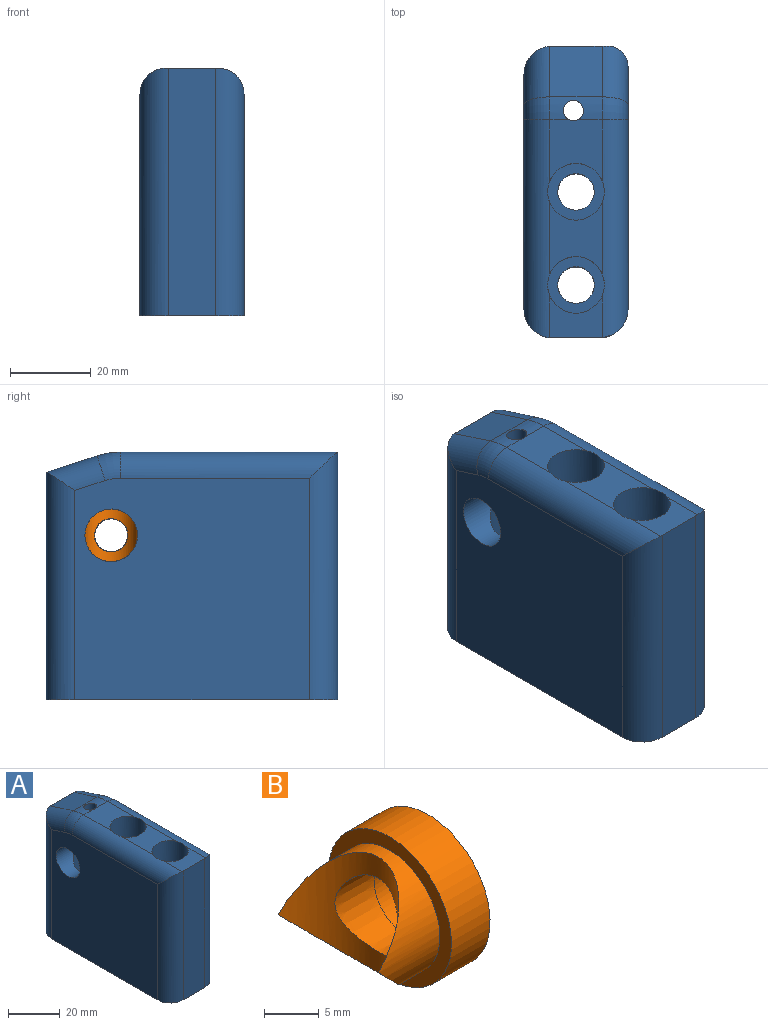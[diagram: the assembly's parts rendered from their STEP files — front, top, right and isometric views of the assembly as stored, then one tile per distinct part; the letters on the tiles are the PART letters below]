
ASSEMBLY  parts=2 mates=1
PART A: 32 faces, bbox 25.7x72.1x61.3 mm
  f0: cylinder r=6.5mm len=20.6mm, axis (1,0,0), area 651.4mm2, adj f1,f28,f29,f30,f31
  f1: cylinder r=2.5mm len=14mm, axis (0,0,-1), area 218.8mm2, adj f0,f2,f27
  f2: plane 15.04x12.9mm, normal (0,0,1), area 153.9mm2, adj f1,f3,f25,f26,f27
  f3: cylinder r=6.4mm len=53.73mm, axis (0,-1,0), area 505.1mm2, adj f2,f4,f19,f21,f22,f23,f24,f25
  f4: torus R=12mm, axis (-1,0,0), area 50.6mm2, adj f3,f5,f19,f27
  f5: cylinder r=6.4mm len=14.61mm, axis (0,-0.95,0.31), area 123.6mm2, adj f4,f6,f17,f18,f19
  f6: plane 12.9x12.58mm, normal (0,0.31,0.95), area 170.5mm2, adj f5,f7,f9,f17,f27
  f7: cylinder r=6.4mm len=14.52mm, axis (0,0.95,-0.31), area 106.2mm2, adj f6,f8,f9,f31
  f8: torus R=12mm, axis (1,0,0), area 50.6mm2, adj f7,f26,f27,f31
  f9: cylinder r=7mm len=56.14mm, axis (0,0,-1), area 600.7mm2, adj f6,f7,f10,f17,f31
  f10: plane 72x25.7mm, normal (0,0,-1), area 1553.5mm2, adj f9,f11,f13,f15,f16,f17,f18,f19
  f11: cylinder r=4.5mm len=45mm, axis (0,0,-1), area 1272.3mm2, adj f10,f12
  f12: plane 14x14mm, normal (0,0,1), area 90.3mm2, adj f11,f25
  f13: cylinder r=4.5mm len=45mm, axis (0,0,-1), area 1272.3mm2, adj f10,f14
  f14: plane 14x14mm, normal (0,0,1), area 90.3mm2, adj f13,f23
  f15: cylinder r=7mm len=61.09mm, axis (0,0,-1), area 647.4mm2, adj f10,f16,f22,f26,f31
  f16: plane 61.09x11.7mm, normal (0,-1,0), area 714.8mm2, adj f10,f15,f21,f22
  f17: plane 56.15x13.73mm, normal (0,1,0), area 768.9mm2, adj f5,f6,f9,f10,f18
  f18: cylinder r=5mm len=55.97mm, axis (0,0,-1), area 420.1mm2, adj f5,f10,f17,f19
  f19: plane 60x54.69mm, normal (1,0,0), area 3046.8mm2, adj f3,f4,f5,f10,f18,f20,f21
  f20: cylinder r=8.25mm len=16.5mm, axis (1,0,0), area 264.4mm2, adj f19,f29
  f21: cylinder r=7mm len=61.09mm, axis (0,0,-1), area 647.4mm2, adj f3,f10,f16,f19,f22
  f22: plane 12.9x10.28mm, normal (0,0,1), area 92.7mm2, adj f3,f15,f16,f21,f23,f26
  f23: cylinder r=7mm len=16.09mm, axis (0,0,-1), area 707.9mm2, adj f3,f14,f22,f24,f26
  f24: plane 17.56x12.9mm, normal (0,0,1), area 146.8mm2, adj f3,f23,f25,f26
  f25: cylinder r=7mm len=16.09mm, axis (0,0,-1), area 707.9mm2, adj f2,f3,f12,f24,f26
  f26: cylinder r=6.4mm len=53.73mm, axis (0,1,0), area 505.1mm2, adj f2,f8,f15,f22,f23,f24,f25,f31
  f27: cylinder r=18.4mm len=12.9mm, axis (-1,0,0), area 55.5mm2, adj f1,f2,f4,f6,f8
  f28: cone r=6.5mm half-angle=45deg, axis (0,0,-1), area 0mm2, adj f0,f30
  f29: plane 16.5x16.5mm, normal (1,0,0), area 81.1mm2, adj f0,f20
  f30: cylinder r=6.5mm len=41mm, axis (0,0,1), area 1490.4mm2, adj f0,f10,f28
  f31: plane 58x54.69mm, normal (-1,0,0), area 3025.2mm2, adj f0,f7,f8,f9,f10,f15,f26
PART B: 7 faces, bbox 13x16x16 mm
  f0: cylinder r=6.5mm len=13mm, axis (-1,0,0), area 157.7mm2, adj f2,f6
  f1: cylinder r=8mm len=16mm, axis (1,0,0), area 251.3mm2, adj f2,f3
  f2: plane 16x16mm, normal (-1,0,0), area 68.3mm2, adj f0,f1
  f3: plane 16x16mm, normal (1,0,0), area 149.5mm2, adj f1,f4
  f4: cylinder r=4.05mm len=8.1mm, axis (1,0,0), area 75.7mm2, adj f3,f5
  f5: cone r=4.22mm half-angle=1deg, axis (-1,0,0), area 109mm2, adj f4,f6
  f6: cylinder r=6.5mm len=13.04mm, axis (0,0,1), area 112.3mm2, adj f0,f5
PLACE A t=(-3411.69,169.15,-121.56)mm
PLACE B t=(161.16,31.37,-107.56)mm
MATE cylindrical B.f1 <-> A.f0  axis (1,0,0) through (174.16,31.37,-107.56)mm
